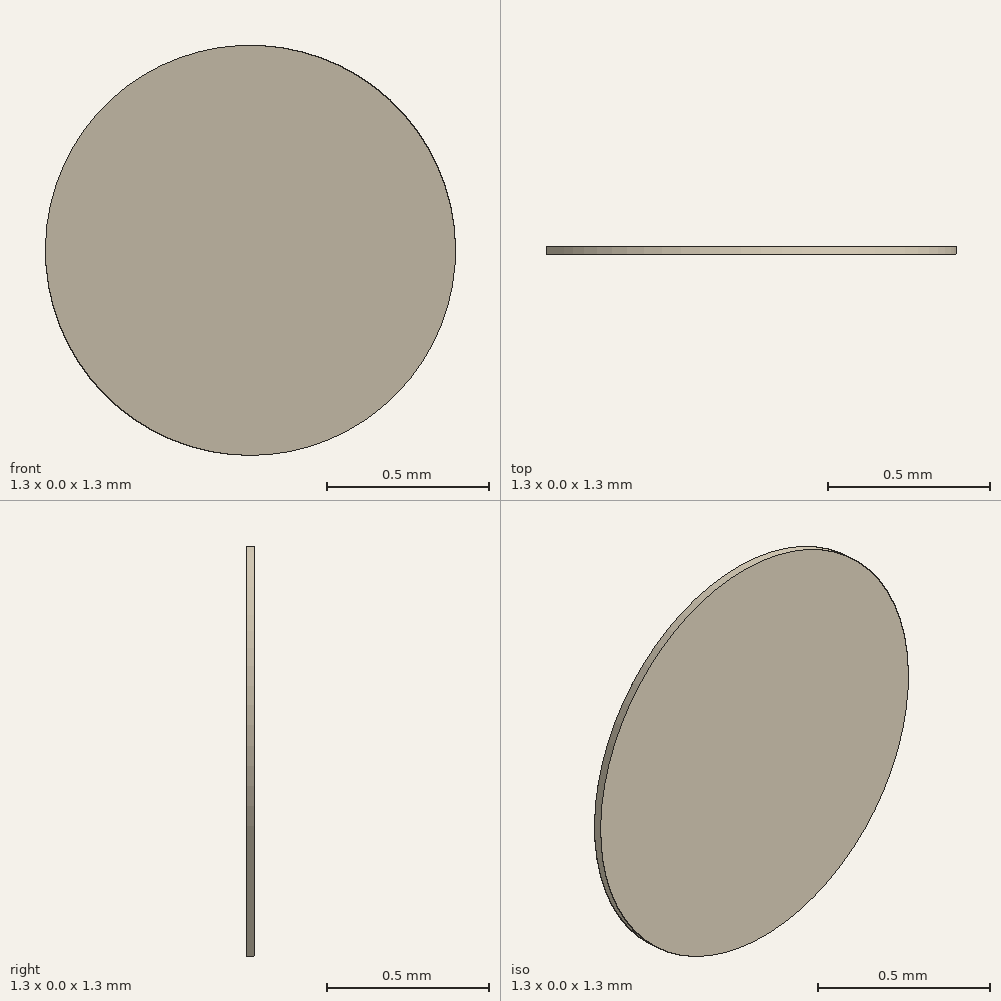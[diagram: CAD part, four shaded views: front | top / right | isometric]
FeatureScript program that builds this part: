
annotation { "Feature Type Name" : "Feature", "Feature Type Description" : "" }
export const myFeature = defineFeature(function(context is Context, id is Id, definition is map)
    precondition{}
    {
        {
            var Q0;
            Q0=qCreatedBy(makeId("Front.planeOp"),FACE);
            var sketch = newSketch(context, id + "F0", { "sketchPlane" : qUnion([Q0])});
            skCircle(sketch, "E0", {"center": v(0, 0) * mm, "radius": 0.64 * mm});
            skSolve(sketch);
        }
        {
            var Q0;
            Q0 = qSketchRegion(id + "F0", true);
            extrude(context, id + "F1", {"entities" : qUnion([Q0]), "depth" : 0.03 * mm});
        }
    });
